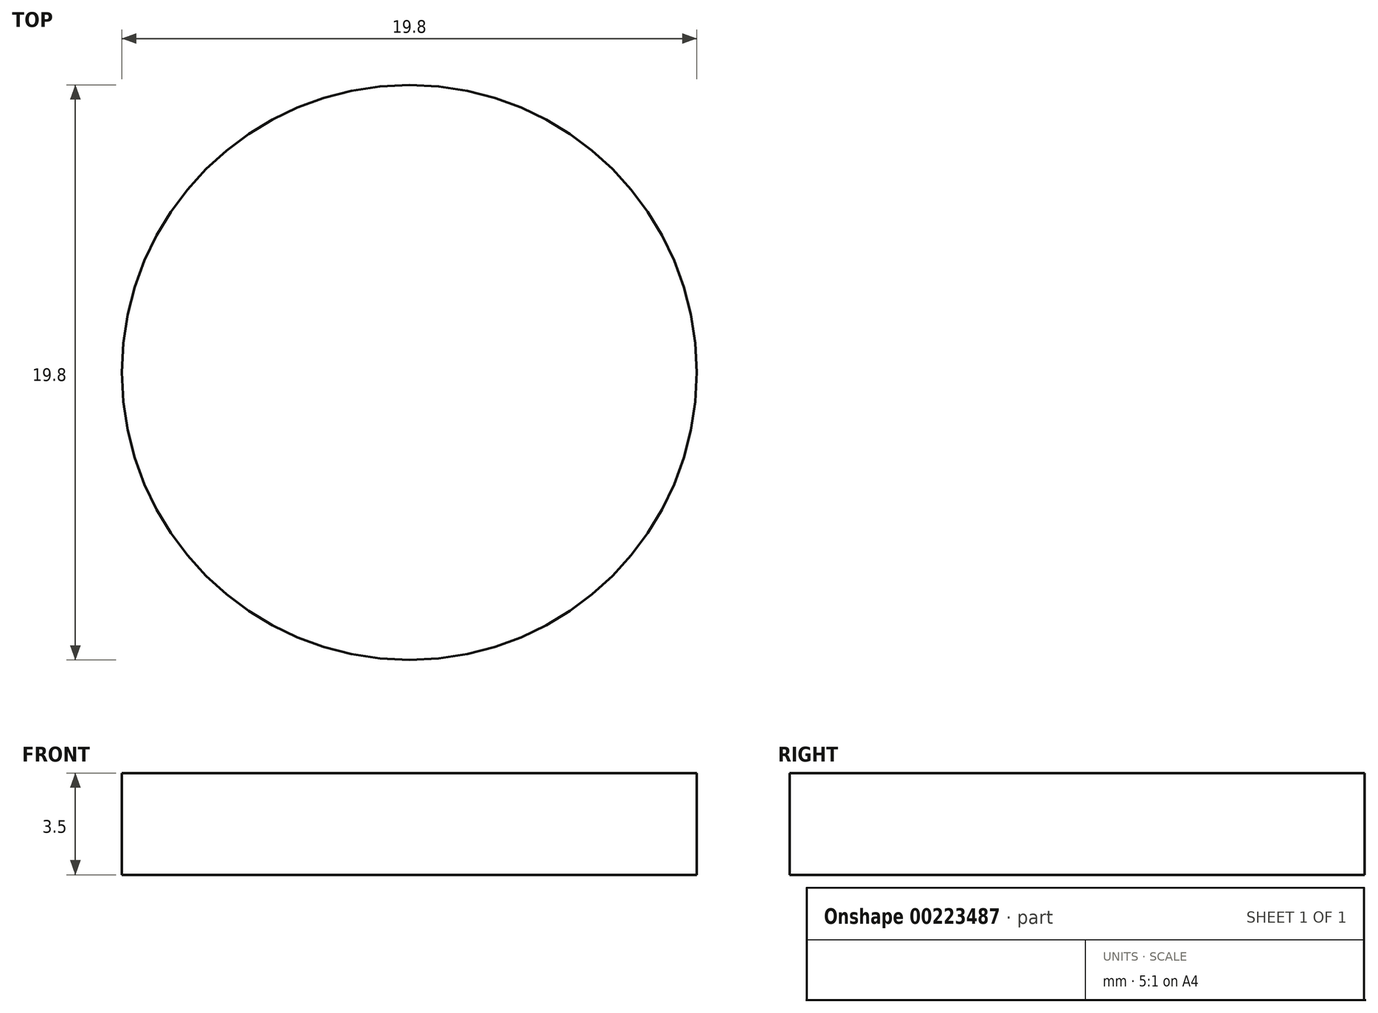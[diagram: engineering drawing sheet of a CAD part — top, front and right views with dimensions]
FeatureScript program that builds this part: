
annotation { "Feature Type Name" : "Feature", "Feature Type Description" : "" }
export const myFeature = defineFeature(function(context is Context, id is Id, definition is map)
    precondition{}
    {
        {
            assignVariable(context, id + "F0", {"name" : "PlungerHeight", "anyValue" : 6 - 2.5});
        }
        {
            var Q0;
            Q0=qCreatedBy(makeId("Top.planeOp"),FACE);
            var sketch = newSketch(context, id + "F1", { "sketchPlane" : qUnion([Q0])});
            skCircle(sketch, "E0", {"center": v(0, 0) * mm, "radius": 9.9 * mm});
            skSolve(sketch);
        }
        {
            var Q0;
            Q0 = qSketchRegion(id + "F1", true);
            extrude(context, id + "F2", {"entities" : qUnion([Q0]), "depth" : (getVariable(context, 'PlungerHeight')) * mm});
        }
    });
